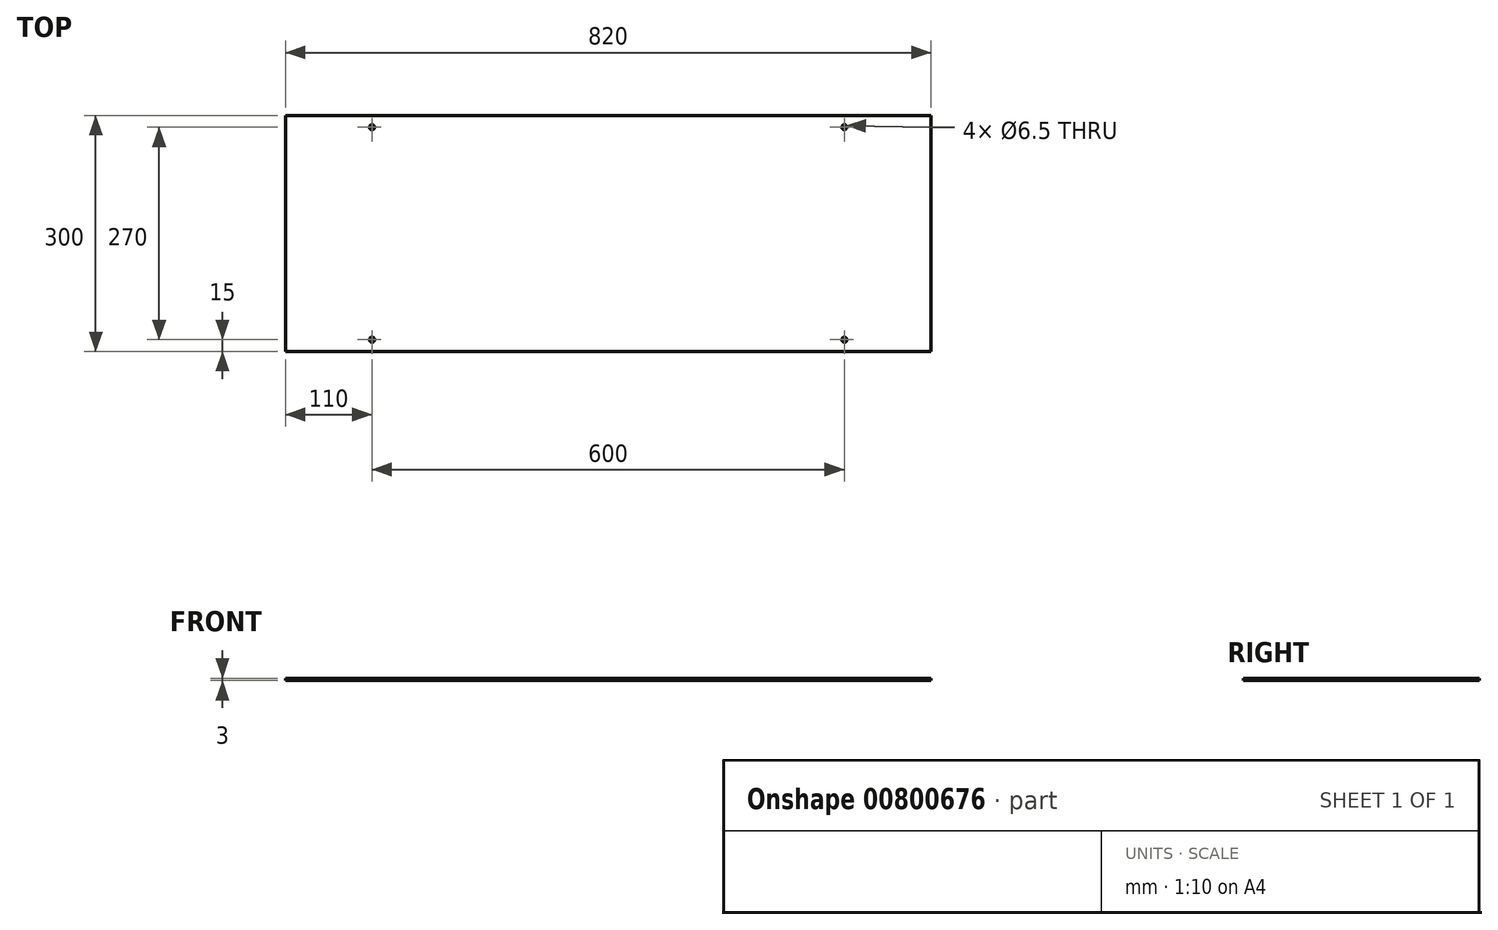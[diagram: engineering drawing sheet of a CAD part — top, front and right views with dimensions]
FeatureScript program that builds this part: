
annotation { "Feature Type Name" : "Feature", "Feature Type Description" : "" }
export const myFeature = defineFeature(function(context is Context, id is Id, definition is map)
    precondition{}
    {
        {
            var Q0;
            Q0=qCreatedBy(makeId("Top.planeOp"),FACE);
            var sketch = newSketch(context, id + "F0", { "sketchPlane" : qUnion([Q0])});
            skLineSegment(sketch, "E0.bottom", {"start": v(410, 150) * mm, "end": v(-410, 150) * mm});
            skLineSegment(sketch, "E0.top", {"start": v(410, -150) * mm, "end": v(-410, -150) * mm});
            skLineSegment(sketch, "E0.left", {"start": v(410, 150) * mm, "end": v(410, -150) * mm});
            skLineSegment(sketch, "E0.right", {"start": v(-410, 150) * mm, "end": v(-410, -150) * mm});
            skPoint(sketch, "E0.middle", {"position": v(0, 0) * mm});
            skSolve(sketch);
        }
        {
            var Q0;
            Q0 = qSketchRegion(id + "F0", true);
            extrude(context, id + "F1", {"entities" : qUnion([Q0]), "depth" : 3 * mm, "offsetDistance" : 25 * mm});
        }
        {
            var Q0;
            Q0=makeQuery(id+"F1.opExtrude","CAP_FACE",FACE,{"disambiguationData":[OSD([sQuery(id+"F0.wireOp",EDGE,"E0.bottom"),sQuery(id+"F0.wireOp",EDGE,"E0.top"),sQuery(id+"F0.wireOp",EDGE,"E0.left"),sQuery(id+"F0.wireOp",EDGE,"E0.right")])],"isStart":true});
            var sketch = newSketch(context, id + "F2", { "sketchPlane" : qUnion([Q0])});
            skLineSegment(sketch, "E1.bottom", {"start": v(-300, 135) * mm, "end": v(300, 135) * mm});
            skLineSegment(sketch, "E1.top", {"start": v(-300, -135) * mm, "end": v(300, -135) * mm});
            skLineSegment(sketch, "E1.left", {"start": v(-300, 135) * mm, "end": v(-300, -135) * mm});
            skLineSegment(sketch, "E1.right", {"start": v(300, 135) * mm, "end": v(300, -135) * mm});
            skPoint(sketch, "E1.middle", {"position": v(0, 0) * mm});
            skSolve(sketch);
        }
        {
            var Q0;
            Q0=sQuery(id+"F2.wireOp",VERTEX,"E1.bottom.start");
            var Q1;
            Q1=sQuery(id+"F2.wireOp",VERTEX,"E1.top.start");
            var Q2;
            Q2=sQuery(id+"F2.wireOp",VERTEX,"E1.top.end");
            var Q3;
            Q3=sQuery(id+"F2.wireOp",VERTEX,"E1.bottom.end");
            var Q4;
            Q4=makeQuery(id+"F1.opExtrude","SWEPT_BODY",BODY,{"disambiguationData":[OSD([sQuery(id+"F0.wireOp",EDGE,"E0.bottom"),sQuery(id+"F0.wireOp",EDGE,"E0.top"),sQuery(id+"F0.wireOp",EDGE,"E0.left"),sQuery(id+"F0.wireOp",EDGE,"E0.right")])]});
            hole(context, id + "F3", {"style" : HoleStyle.SIMPLE, "endStyle" : HoleEndStyle.THROUGH, "holeDiameter" : 6.5 * mm, "majorDiameter" : 5 * mm, "isTappedThrough" : true, "tappedDepth" : 12 * mm, "tapClearance" : 3, "locations" : qUnion([Q0, Q1, Q2, Q3]), "scope" : qUnion([Q4])});
        }
    });
